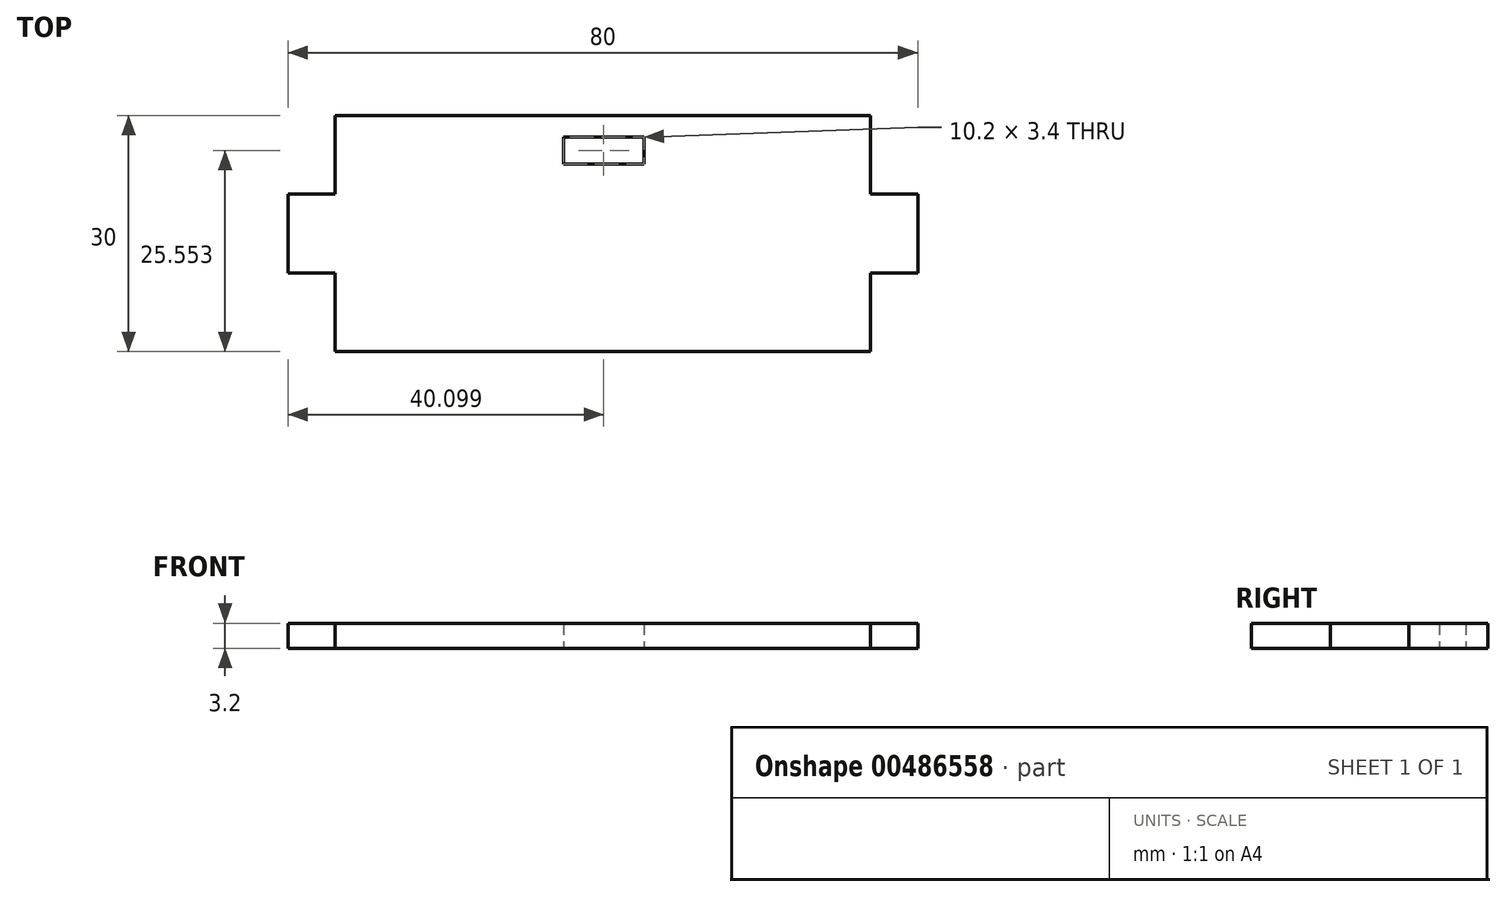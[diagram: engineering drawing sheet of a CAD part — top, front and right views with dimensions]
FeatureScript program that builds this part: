
annotation { "Feature Type Name" : "Feature", "Feature Type Description" : "" }
export const myFeature = defineFeature(function(context is Context, id is Id, definition is map)
    precondition{}
    {
        {
            var Q0;
            Q0=qCreatedBy(makeId("Top.planeOp"),FACE);
            var sketch = newSketch(context, id + "F0", { "sketchPlane" : qUnion([Q0])});
            skLineSegment(sketch, "E0.bottom", {"start": v(-29.98, 10) * mm, "end": v(38.02, 10) * mm});
            skLineSegment(sketch, "E0.top", {"start": v(-29.98, -20) * mm, "end": v(38.02, -20) * mm});
            skLineSegment(sketch, "E0.left", {"start": v(-29.98, 10) * mm, "end": v(-29.98, -20) * mm});
            skLineSegment(sketch, "E0.right", {"start": v(38.02, 10) * mm, "end": v(38.02, -20) * mm});
            skLineSegment(sketch, "E1", {"start": v(38.02, 0) * mm, "end": v(44.02, 0) * mm});
            skLineSegment(sketch, "E2", {"start": v(44.02, 0) * mm, "end": v(44.02, -10) * mm});
            skLineSegment(sketch, "E3", {"start": v(44.02, -10) * mm, "end": v(38.02, -10) * mm});
            skLineSegment(sketch, "E4", {"start": v(-29.98, 0) * mm, "end": v(-35.98, 0) * mm});
            skLineSegment(sketch, "E5", {"start": v(-35.98, 0) * mm, "end": v(-35.98, -10) * mm});
            skLineSegment(sketch, "E6", {"start": v(-35.98, -10) * mm, "end": v(-29.98, -10) * mm});
            skLineSegment(sketch, "E7.bottom", {"start": v(9.22, 3.85) * mm, "end": v(-0.98, 3.85) * mm});
            skLineSegment(sketch, "E7.top", {"start": v(9.22, 7.25) * mm, "end": v(-0.98, 7.25) * mm});
            skLineSegment(sketch, "E7.left", {"start": v(9.22, 3.85) * mm, "end": v(9.22, 7.25) * mm});
            skLineSegment(sketch, "E7.right", {"start": v(-0.98, 3.85) * mm, "end": v(-0.98, 7.25) * mm});
            skPoint(sketch, "E7.middle", {"position": v(4.12, 5.55) * mm});
            skSolve(sketch);
        }
        {
            var Q0;
            Q0 = qSketchRegion(id + "F0", true);
            extrude(context, id + "F1", {"entities" : qUnion([Q0]), "depth" : 3.2 * mm, "offsetDistance" : 25 * mm});
        }
    });
